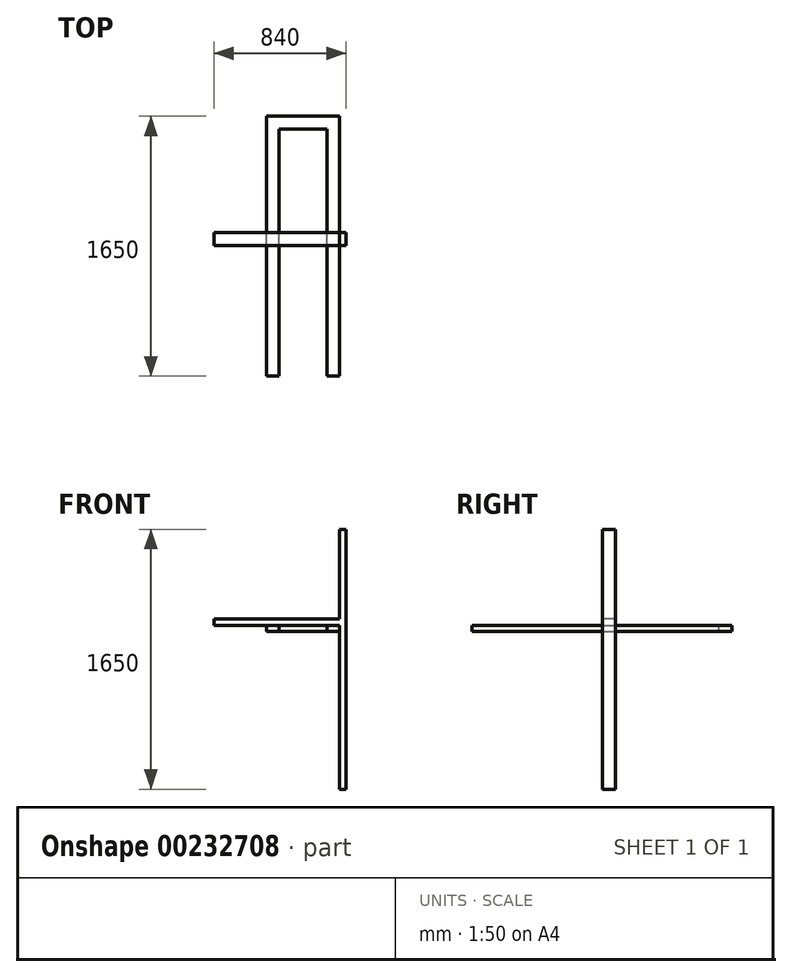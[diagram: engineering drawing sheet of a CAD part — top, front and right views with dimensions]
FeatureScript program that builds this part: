
annotation { "Feature Type Name" : "Feature", "Feature Type Description" : "" }
export const myFeature = defineFeature(function(context is Context, id is Id, definition is map)
    precondition{}
    {
        {
            var Q0;
            Q0=qCreatedBy(makeId("Right.planeOp"),FACE);
            var sketch = newSketch(context, id + "F0", { "sketchPlane" : qUnion([Q0])});
            skLineSegment(sketch, "E0.bottom", {"start": v(0, 0) * mm, "end": v(80, 0) * mm});
            skLineSegment(sketch, "E0.top", {"start": v(0, 1650) * mm, "end": v(80, 1650) * mm});
            skLineSegment(sketch, "E0.left", {"start": v(0, 0) * mm, "end": v(0, 1650) * mm});
            skLineSegment(sketch, "E0.right", {"start": v(80, 0) * mm, "end": v(80, 1650) * mm});
            skSolve(sketch);
        }
        {
            var Q0;
            Q0 = qSketchRegion(id + "F0", true);
            extrude(context, id + "F1", {"entities" : qUnion([Q0]), "oppositeDirection" : true, "depth" : 40 * mm});
        }
        {
            var Q0;
            Q0=makeQuery(id+"F1.opExtrude","CAP_FACE",FACE,{"disambiguationData":[OSD([sQuery(id+"F0.wireOp",EDGE,"E0.bottom"),sQuery(id+"F0.wireOp",EDGE,"E0.top"),sQuery(id+"F0.wireOp",EDGE,"E0.left"),sQuery(id+"F0.wireOp",EDGE,"E0.right")])],"isStart":false});
            var sketch = newSketch(context, id + "F2", { "sketchPlane" : qUnion([Q0])});
            skLineSegment(sketch, "E1.bottom", {"start": v(-80, 1082) * mm, "end": v(0, 1082) * mm});
            skLineSegment(sketch, "E1.top", {"start": v(-80, 1042) * mm, "end": v(0, 1042) * mm});
            skLineSegment(sketch, "E1.left", {"start": v(-80, 1082) * mm, "end": v(-80, 1042) * mm});
            skLineSegment(sketch, "E1.right", {"start": v(0, 1082) * mm, "end": v(0, 1042) * mm});
            skSolve(sketch);
        }
        {
            var Q0;
            Q0 = qSketchRegion(id + "F2", true);
            extrude(context, id + "F3", {"entities" : qUnion([Q0]), "operationType" : NewBodyOperationType.ADD, "depth" : 800 * mm});
        }
        {
            var Q0;
            Q0=makeQuery(id+"F3.opExtrude","SWEPT_FACE",FACE,{"disambiguationData":[OSD([sQuery(id+"F2.wireOp",EDGE,"E1.top")])]});
            var sketch = newSketch(context, id + "F4", { "sketchPlane" : qUnion([Q0])});
            skPoint(sketch, "E2.firstSnap0", {"position": v(-40, -40) * mm});
            skLineSegment(sketch, "E2.bottom", {"start": v(-40, 830) * mm, "end": v(-120, 830) * mm});
            skLineSegment(sketch, "E2.top", {"start": v(-40, -820) * mm, "end": v(-505, -820) * mm});
            skLineSegment(sketch, "E2.left", {"start": v(-40, 830) * mm, "end": v(-40, -820) * mm});
            skLineSegment(sketch, "E2.right", {"start": v(-505, 830) * mm, "end": v(-505, -820) * mm});
            skLineSegment(sketch, "E3.top", {"start": v(-425, -740) * mm, "end": v(-120, -740) * mm});
            skLineSegment(sketch, "E3.left", {"start": v(-425, 830) * mm, "end": v(-425, -740) * mm});
            skLineSegment(sketch, "E3.right", {"start": v(-120, 830) * mm, "end": v(-120, -740) * mm});
            skLineSegment(sketch, "E4.trimOffspring", {"start": v(-425, 830) * mm, "end": v(-505, 830) * mm});
            skSolve(sketch);
        }
        {
            var Q0;
            Q0 = qSketchRegion(id + "F4", true);
            extrude(context, id + "F5", {"entities" : qUnion([Q0]), "operationType" : NewBodyOperationType.ADD, "depth" : 40 * mm});
        }
    });
